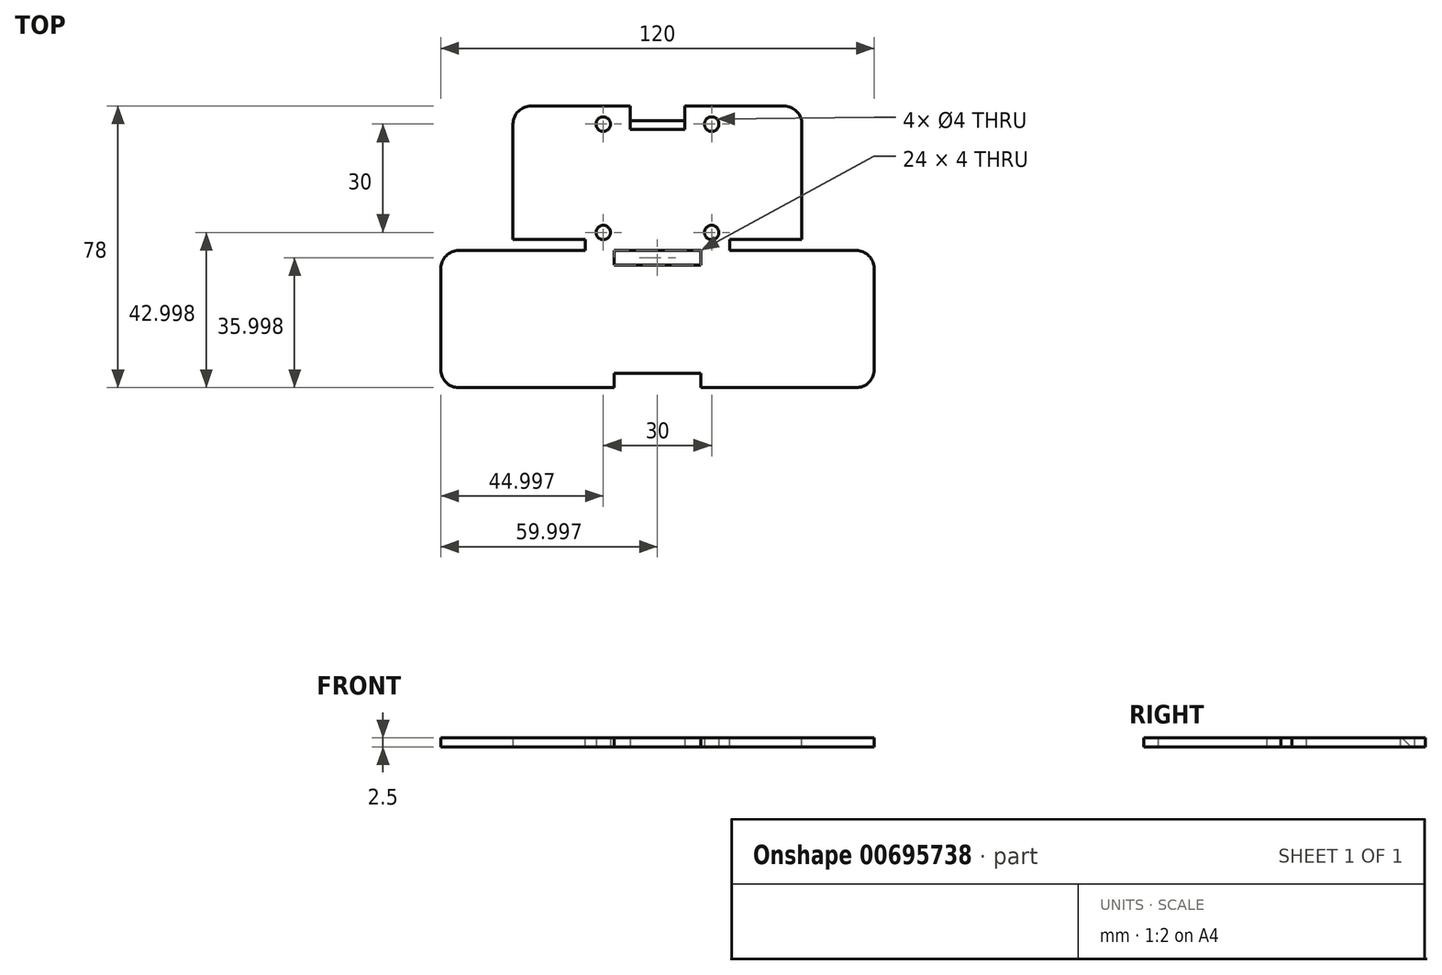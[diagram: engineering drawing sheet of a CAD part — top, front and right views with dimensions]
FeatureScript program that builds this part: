
annotation { "Feature Type Name" : "Feature", "Feature Type Description" : "" }
export const myFeature = defineFeature(function(context is Context, id is Id, definition is map)
    precondition{}
    {
        {
            var Q0;
            Q0=qCreatedBy(makeId("Top.planeOp"),FACE);
            var sketch = newSketch(context, id + "F0", { "sketchPlane" : qUnion([Q0])});
            skLineSegment(sketch, "E0.bottom", {"start": v(-51.88, 6.2) * mm, "end": v(-16.88, 6.2) * mm});
            skLineSegment(sketch, "E0.top", {"start": v(-51.88, -31.8) * mm, "end": v(58.12, -31.8) * mm});
            skLineSegment(sketch, "E0.left", {"start": v(-56.88, 1.2) * mm, "end": v(-56.88, -26.8) * mm});
            skLineSegment(sketch, "E0.right", {"start": v(63.12, 1.2) * mm, "end": v(63.12, -26.8) * mm});
            skLineSegment(sketch, "E1", {"start": v(-16.88, 6.2) * mm, "end": v(-16.88, 41.2) * mm});
            skLineSegment(sketch, "E2", {"start": v(-11.88, 46.2) * mm, "end": v(18.12, 46.2) * mm});
            skLineSegment(sketch, "E3", {"start": v(23.12, 41.2) * mm, "end": v(23.12, 6.2) * mm});
            skCircle(sketch, "E4", {"center": v(-11.88, 41.2) * mm, "radius": 2 * mm});
            skCircle(sketch, "E5", {"center": v(18.12, 41.2) * mm, "radius": 2 * mm});
            skCircle(sketch, "E6", {"center": v(-11.88, 11.2) * mm, "radius": 2 * mm});
            skCircle(sketch, "E7", {"center": v(18.12, 11.2) * mm, "radius": 2 * mm});
            skLineSegment(sketch, "E8", {"start": v(-8.88, -31.8) * mm, "end": v(-8.88, -27.8) * mm});
            skLineSegment(sketch, "E9", {"start": v(-8.88, -27.8) * mm, "end": v(15.12, -27.8) * mm});
            skLineSegment(sketch, "E10", {"start": v(15.12, -27.8) * mm, "end": v(15.12, -31.8) * mm});
            skLineSegment(sketch, "E11.bottom", {"start": v(-8.88, 6.2) * mm, "end": v(15.12, 6.2) * mm});
            skLineSegment(sketch, "E11.top", {"start": v(-8.88, 2.2) * mm, "end": v(15.12, 2.2) * mm});
            skLineSegment(sketch, "E11.left", {"start": v(-8.88, 6.2) * mm, "end": v(-8.88, 2.2) * mm});
            skLineSegment(sketch, "E11.right", {"start": v(15.12, 6.2) * mm, "end": v(15.12, 2.2) * mm});
            skPoint(sketch, "E12", {"position": v(3.12, -31.8) * mm});
            skPoint(sketch, "E13", {"position": v(3.12, -27.8) * mm});
            skPoint(sketch, "E14", {"position": v(3.12, 46.2) * mm});
            skLineSegment(sketch, "E15", {"start": v(-11.88, 41.2) * mm, "end": v(18.12, 41.2) * mm, "construction": true});
            skPoint(sketch, "E16", {"position": v(3.12, 41.2) * mm});
            skPoint(sketch, "E17.visualSharp", {"position": v(-56.88, 6.2) * mm});
            skArc(sketch, "E17.filletArc", {"start": v(-51.88, 6.2) * mm, "mid": v(-55.42, 4.73) * mm, "end": v(-56.88, 1.2) * mm});
            skPoint(sketch, "E18.visualSharp", {"position": v(-56.88, -31.8) * mm});
            skArc(sketch, "E18.filletArc", {"start": v(-56.88, -26.8) * mm, "mid": v(-55.42, -30.34) * mm, "end": v(-51.88, -31.8) * mm});
            skPoint(sketch, "E19.visualSharp", {"position": v(63.12, -31.8) * mm});
            skArc(sketch, "E19.filletArc", {"start": v(58.12, -31.8) * mm, "mid": v(61.65, -30.34) * mm, "end": v(63.12, -26.8) * mm});
            skPoint(sketch, "E20.visualSharp", {"position": v(63.12, 6.2) * mm});
            skArc(sketch, "E20.filletArc", {"start": v(63.12, 1.2) * mm, "mid": v(61.65, 4.73) * mm, "end": v(58.12, 6.2) * mm});
            skPoint(sketch, "E21.visualSharp", {"position": v(23.12, 46.2) * mm});
            skArc(sketch, "E21.filletArc", {"start": v(23.12, 41.2) * mm, "mid": v(21.65, 44.73) * mm, "end": v(18.12, 46.2) * mm});
            skPoint(sketch, "E22.visualSharp", {"position": v(-16.88, 46.2) * mm});
            skArc(sketch, "E22.filletArc", {"start": v(-11.88, 46.2) * mm, "mid": v(-15.42, 44.73) * mm, "end": v(-16.88, 41.2) * mm});
            skLineSegment(sketch, "E23.trimOffspring", {"start": v(23.12, 6.2) * mm, "end": v(58.12, 6.2) * mm});
            skLineSegment(sketch, "E24", {"start": v(-16.88, 46.2) * mm, "end": v(-31.88, 46.2) * mm});
            skLineSegment(sketch, "E25", {"start": v(-36.88, 41.2) * mm, "end": v(-36.88, 6.2) * mm});
            skLineSegment(sketch, "E26", {"start": v(3.12, 46.2) * mm, "end": v(3.12, -27.8) * mm, "construction": true});
            skLineSegment(sketch, "E27", {"start": v(-16.88, 46.2) * mm, "end": v(-11.88, 46.2) * mm});
            skLineSegment(sketch, "E28.MirrorCS", {"start": v(43.12, 41.2) * mm, "end": v(43.12, 6.2) * mm});
            skLineSegment(sketch, "E29.MirrorCS", {"start": v(23.12, 46.2) * mm, "end": v(38.12, 46.2) * mm});
            skLineSegment(sketch, "E30.MirrorCS", {"start": v(23.12, 46.2) * mm, "end": v(18.12, 46.2) * mm});
            skPoint(sketch, "E31.visualSharp", {"position": v(-36.88, 46.2) * mm});
            skArc(sketch, "E31.filletArc", {"start": v(-31.88, 46.2) * mm, "mid": v(-35.42, 44.73) * mm, "end": v(-36.88, 41.2) * mm});
            skPoint(sketch, "E32.visualSharp", {"position": v(43.12, 46.2) * mm});
            skArc(sketch, "E32.filletArc", {"start": v(43.12, 41.2) * mm, "mid": v(41.65, 44.73) * mm, "end": v(38.12, 46.2) * mm});
            skLineSegment(sketch, "E33.bottom", {"start": v(10.62, 50.2) * mm, "end": v(-4.38, 50.2) * mm});
            skLineSegment(sketch, "E33.top", {"start": v(10.62, 42.2) * mm, "end": v(-4.38, 42.2) * mm});
            skLineSegment(sketch, "E33.left", {"start": v(10.62, 50.2) * mm, "end": v(10.62, 42.2) * mm});
            skLineSegment(sketch, "E33.right", {"start": v(-4.38, 50.2) * mm, "end": v(-4.38, 42.2) * mm});
            skSolve(sketch);
        }
        {
            var Q0;
            Q0=makeQuery(id+"F0.imprint","IMPRINT",FACE,{"disambiguationData":[TD([[makeQuery(id+"F0.imprint","IMPRINT",EDGE,{"derivedFrom":sQuery(id+"F0.wireOp",EDGE,"E0.bottom")}),-1.0]])]});
            var Q1;
            {var subQ0=sQuery(id+"F0.wireOp",EDGE,"E1");Q1=makeQuery(id+"F0.imprint","IMPRINT",FACE,{"disambiguationData":[TD([[makeQuery(id+"F0.imprint","IMPRINT",EDGE,{"derivedFrom":subQ0}),1.0]])]});}
            var Q2;
            {var subQ2=sQuery(id+"F0.wireOp",EDGE,"E3");Q2=makeQuery(id+"F0.imprint","IMPRINT",FACE,{"disambiguationData":[TD([[makeQuery(id+"F0.imprint","IMPRINT",EDGE,{"derivedFrom":subQ2}),1.0]])]});}
            extrude(context, id + "F1", {"entities" : qUnion([Q0, Q1, Q2]), "depth" : 2.5 * mm, "offsetDistance" : 25 * mm});
        }
        {
            var Q0;
            Q0=makeQuery(id+"F1.opExtrude","CAP_FACE",FACE,{"disambiguationData":[OSD([sQuery(id+"F0.wireOp",EDGE,"E0.bottom"),sQuery(id+"F0.wireOp",EDGE,"E0.top"),sQuery(id+"F0.wireOp",EDGE,"E0.left"),sQuery(id+"F0.wireOp",EDGE,"E0.right"),sQuery(id+"F0.wireOp",EDGE,"E2"),sQuery(id+"F0.wireOp",EDGE,"E4"),sQuery(id+"F0.wireOp",EDGE,"E5"),sQuery(id+"F0.wireOp",EDGE,"E6"),sQuery(id+"F0.wireOp",EDGE,"E7"),sQuery(id+"F0.wireOp",EDGE,"E8"),sQuery(id+"F0.wireOp",EDGE,"E9"),sQuery(id+"F0.wireOp",EDGE,"E10"),sQuery(id+"F0.wireOp",EDGE,"E11.bottom"),sQuery(id+"F0.wireOp",EDGE,"E11.top"),sQuery(id+"F0.wireOp",EDGE,"E11.left"),sQuery(id+"F0.wireOp",EDGE,"E11.right"),sQuery(id+"F0.wireOp",EDGE,"E17.filletArc"),sQuery(id+"F0.wireOp",EDGE,"E18.filletArc"),sQuery(id+"F0.wireOp",EDGE,"E19.filletArc"),sQuery(id+"F0.wireOp",EDGE,"E20.filletArc"),sQuery(id+"F0.wireOp",EDGE,"E23.trimOffspring"),sQuery(id+"F0.wireOp",EDGE,"E24"),sQuery(id+"F0.wireOp",EDGE,"E25"),sQuery(id+"F0.wireOp",EDGE,"E27"),sQuery(id+"F0.wireOp",EDGE,"E28.MirrorCS"),sQuery(id+"F0.wireOp",EDGE,"E29.MirrorCS"),sQuery(id+"F0.wireOp",EDGE,"E30.MirrorCS"),sQuery(id+"F0.wireOp",EDGE,"E31.filletArc"),sQuery(id+"F0.wireOp",EDGE,"E32.filletArc"),sQuery(id+"F0.wireOp",EDGE,"E33.top"),sQuery(id+"F0.wireOp",EDGE,"E33.left"),sQuery(id+"F0.wireOp",EDGE,"E33.right")])],"isStart":false});
            var sketch = newSketch(context, id + "F2", { "sketchPlane" : qUnion([Q0])});
            skLineSegment(sketch, "E34.bottom", {"start": v(-36.88, 6.2) * mm, "end": v(-16.88, 6.2) * mm});
            skLineSegment(sketch, "E34.top", {"start": v(-36.88, 9.2) * mm, "end": v(-16.88, 9.2) * mm});
            skLineSegment(sketch, "E34.left", {"start": v(-36.88, 6.2) * mm, "end": v(-36.88, 9.2) * mm});
            skLineSegment(sketch, "E34.right", {"start": v(-16.88, 6.2) * mm, "end": v(-16.88, 9.2) * mm});
            skLineSegment(sketch, "E35.bottom", {"start": v(43.12, 6.2) * mm, "end": v(23.12, 6.2) * mm});
            skLineSegment(sketch, "E35.top", {"start": v(43.12, 9.2) * mm, "end": v(23.12, 9.2) * mm});
            skLineSegment(sketch, "E35.left", {"start": v(43.12, 6.2) * mm, "end": v(43.12, 9.2) * mm});
            skLineSegment(sketch, "E35.right", {"start": v(23.12, 6.2) * mm, "end": v(23.12, 9.2) * mm});
            skSolve(sketch);
        }
        {
            var Q0;
            Q0 = qSketchRegion(id + "F2", true);
            extrude(context, id + "F3", {"entities" : qUnion([Q0]), "operationType" : NewBodyOperationType.REMOVE, "oppositeDirection" : true, "depth" : 25 * mm, "offsetDistance" : 25 * mm});
        }
        {
            var Q0;
            Q0=makeQuery(id+"F1.opExtrude","CAP_EDGE",EDGE,{"disambiguationData":[OSD([sQuery(id+"F0.wireOp",EDGE,"E33.top")])],"isStart":false});
            chamfer(context, id + "F4", {"entities" : qUnion([Q0]), "width" : 2.5 * mm, "tangentPropagation" : true});
        }
    });
